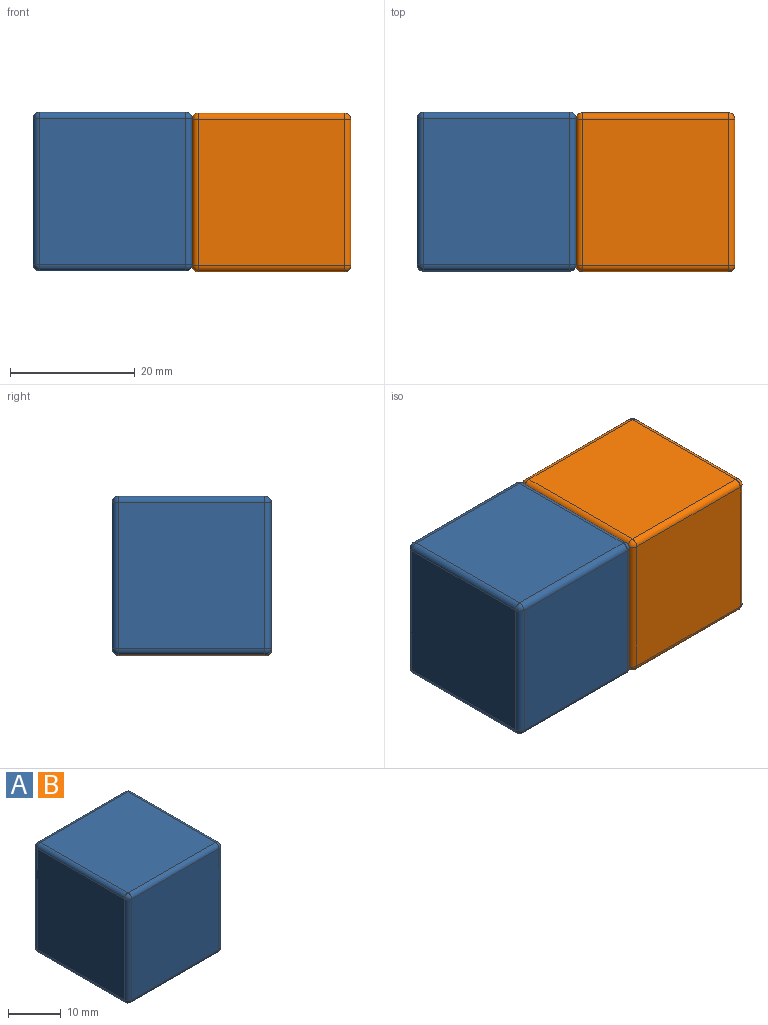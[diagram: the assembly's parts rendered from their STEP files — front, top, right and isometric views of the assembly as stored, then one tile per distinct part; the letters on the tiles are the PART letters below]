
ASSEMBLY  parts=2 mates=1
PART A: 26 faces, bbox 25.4x25.4x25.4 mm
  f0: plane 23.4x23.4mm, normal (0,1,0), area 547.6mm2, adj f14,f19,f22,f25
  f1: plane 23.4x23.4mm, normal (-1,0,0), area 547.6mm2, adj f11,f20,f21,f25
  f2: plane 23.4x23.4mm, normal (0,-1,0), area 547.6mm2, adj f6,f10,f11,f12
  f3: plane 23.4x23.4mm, normal (1,0,0), area 547.6mm2, adj f6,f9,f13,f14
  f4: plane 23.4x23.4mm, normal (0,0,1), area 547.6mm2, adj f9,f10,f19,f20
  f5: plane 23.4x23.4mm, normal (0,0,-1), area 547.6mm2, adj f12,f13,f21,f22
  f6: cylinder r=1mm len=23.4mm, axis (0,0,1), area 36.8mm2, adj f2,f3,f7,f8
  f7: sphere r=1mm, area 1.6mm2, adj f6,f9,f10
  f8: sphere r=1mm, area 1.6mm2, adj f6,f12,f13
  f9: cylinder r=1mm len=23.4mm, axis (0,-1,0), area 36.8mm2, adj f3,f4,f7,f15
  f10: cylinder r=1mm len=23.4mm, axis (-1,0,0), area 36.8mm2, adj f2,f4,f7,f16
  f11: cylinder r=1mm len=23.4mm, axis (0,0,-1), area 36.8mm2, adj f1,f2,f16,f17
  f12: cylinder r=1mm len=23.4mm, axis (1,0,0), area 36.8mm2, adj f2,f5,f8,f17
  f13: cylinder r=1mm len=23.4mm, axis (0,1,0), area 36.8mm2, adj f3,f5,f8,f18
  f14: cylinder r=1mm len=23.4mm, axis (0,0,-1), area 36.8mm2, adj f0,f3,f15,f18
  f15: sphere r=1mm, area 1.6mm2, adj f9,f14,f19
  f16: sphere r=1mm, area 1.6mm2, adj f10,f11,f20
  f17: sphere r=1mm, area 1.6mm2, adj f11,f12,f21
  f18: sphere r=1mm, area 1.6mm2, adj f13,f14,f22
  f19: cylinder r=1mm len=23.4mm, axis (1,0,0), area 36.8mm2, adj f0,f4,f15,f23
  f20: cylinder r=1mm len=23.4mm, axis (0,1,0), area 36.8mm2, adj f1,f4,f16,f23
  f21: cylinder r=1mm len=23.4mm, axis (0,-1,0), area 36.8mm2, adj f1,f5,f17,f24
  f22: cylinder r=1mm len=23.4mm, axis (-1,0,0), area 36.8mm2, adj f0,f5,f18,f24
  f23: sphere r=1mm, area 1.6mm2, adj f19,f20,f25
  f24: sphere r=1mm, area 1.6mm2, adj f21,f22,f25
  f25: cylinder r=1mm len=23.4mm, axis (0,0,1), area 36.8mm2, adj f0,f1,f23,f24
PART B: same geometry as A
PLACE A t=(-22.5,22.67,-11.21)mm
PLACE B t=(2.9,22.55,-11.36)mm
MATE planar A.f3 <-> B.f1  axis (1,0,0) through (2.9,9.97,1.49)mm
